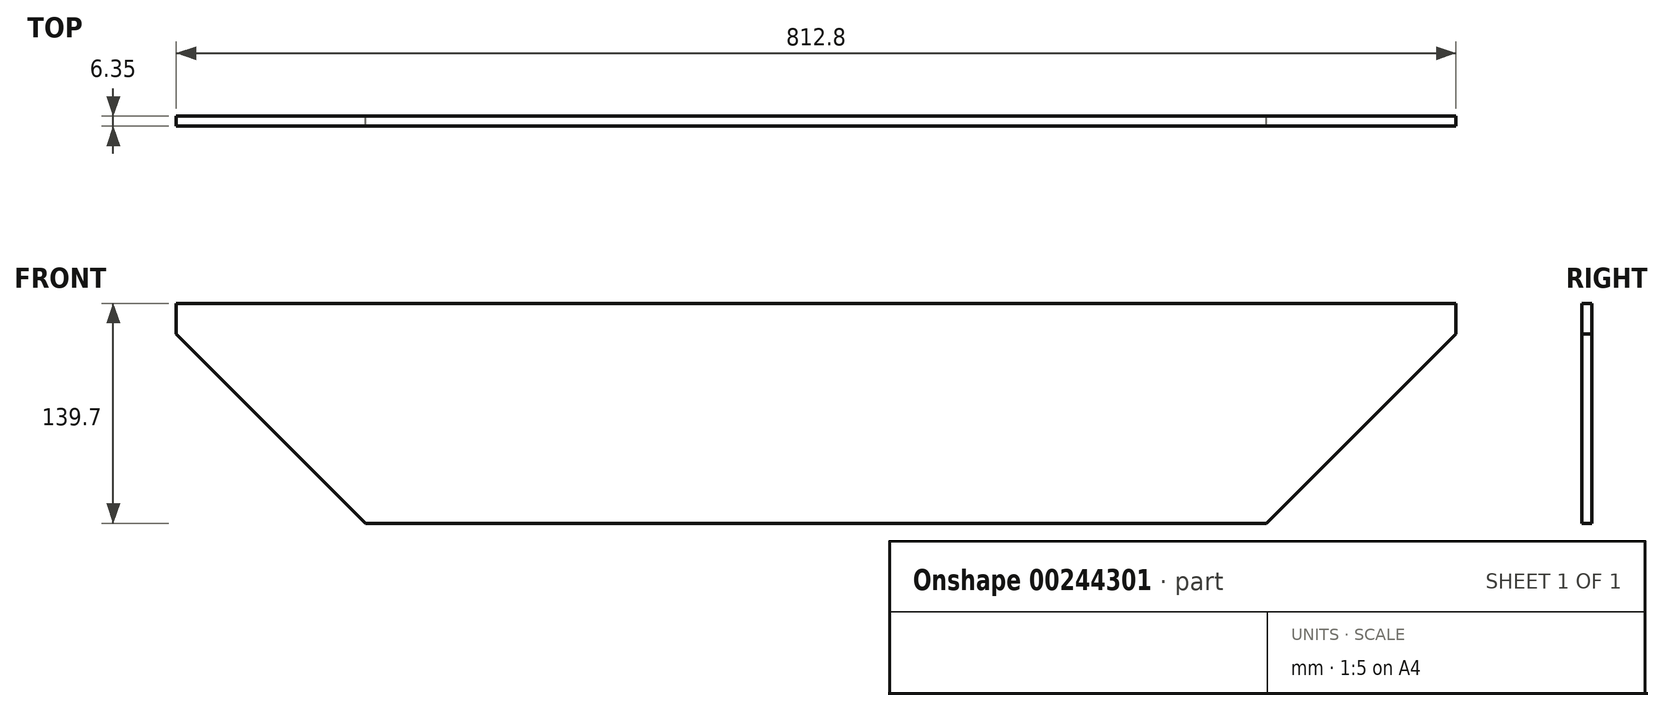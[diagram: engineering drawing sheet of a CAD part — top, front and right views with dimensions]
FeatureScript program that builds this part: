
annotation { "Feature Type Name" : "Feature", "Feature Type Description" : "" }
export const myFeature = defineFeature(function(context is Context, id is Id, definition is map)
    precondition{}
    {
        {
            var Q0;
            Q0=qCreatedBy(makeId("Front.planeOp"),FACE);
            var sketch = newSketch(context, id + "F0", { "sketchPlane" : qUnion([Q0])});
            skLineSegment(sketch, "E0.bottom", {"start": v(-199.12, 62.51) * mm, "end": v(613.68, 62.51) * mm});
            skLineSegment(sketch, "E0.top", {"start": v(-199.12, -77.19) * mm, "end": v(613.68, -77.19) * mm});
            skLineSegment(sketch, "E0.left", {"start": v(-199.12, 62.51) * mm, "end": v(-199.12, -77.19) * mm});
            skLineSegment(sketch, "E0.right", {"start": v(613.68, 62.51) * mm, "end": v(613.68, -77.19) * mm});
            skLineSegment(sketch, "E1", {"start": v(613.68, 43.1) * mm, "end": v(493.4, -77.19) * mm});
            skLineSegment(sketch, "E2", {"start": v(-199.12, 43.1) * mm, "end": v(-78.83, -77.19) * mm});
            skSolve(sketch);
        }
        {
            var Q0;
            Q0=makeQuery(id+"F0.imprint","IMPRINT",FACE,{"disambiguationData":[TD([[makeQuery(id+"F0.imprint","IMPRINT",EDGE,{"derivedFrom":sQuery(id+"F0.wireOp",EDGE,"E0.bottom")}),-1.0]])]});
            extrude(context, id + "F1", {"entities" : qUnion([Q0]), "depth" : 6.35 * mm});
        }
    });
